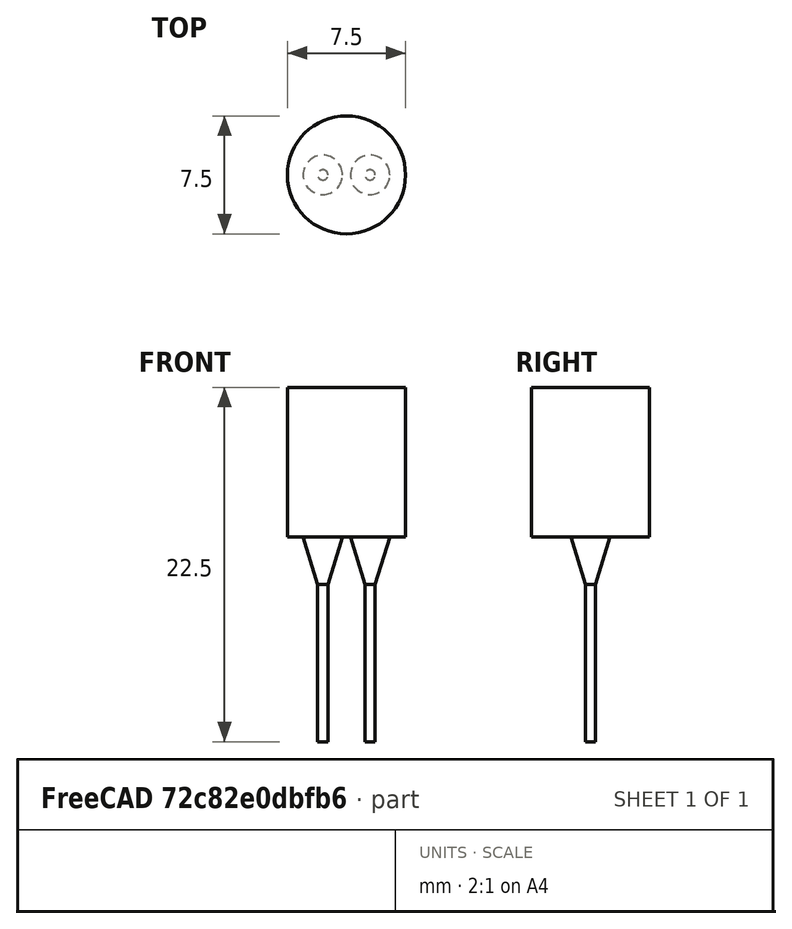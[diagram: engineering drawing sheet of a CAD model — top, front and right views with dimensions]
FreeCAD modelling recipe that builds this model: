
FCSTD DOCUMENT  (FreeCAD 0.19R24366 (Git))
Label:  FERROCORE_COIL0608_inductor_3.0_7.5_9.5
License: All rights reserved
LicenseURL: http://en.wikipedia.org/wiki/All_rights_reserved
objects: Part::Cylinder×3, Part::MultiFuse×3, Part::Cone×2
note: 8 computed .brp shape members not serialized (recipe doc carries the construction recipe); baked Part::Feature solids carry a one-line shape summary decoded from their .brp

FEATURE [Part::Cylinder] Cylinder  label="Henger"
  Angle = 360
  AttacherType = Attacher::AttachEngine3D
  Height = 9.5
  Radius = 3.75
FEATURE [Part::Cone] Cone  label="Kúp"
  Angle = 360
  AttacherType = Attacher::AttachEngine3D
  Height = 3
  Placement = pos=(-9,0,0) rot=(0,0,1;0rad)
  Radius1 = 0.325
  Radius2 = 1.25
FEATURE [Part::Cylinder] Cylinder001  label="Henger001"
  Angle = 360
  AttacherType = Attacher::AttachEngine3D
  Height = 10
  Placement = pos=(-9,0,-10) rot=(0,0,1;0rad)
  Radius = 0.325
FEATURE [Part::MultiFuse] Fusion
  Placement = pos=(10.5,0,-3) rot=(0,0,1;0rad)
  Shapes = -> [Cone,Cylinder001]
FEATURE [Part::Cone] Cone001  label="Kúp001"
  Angle = 360
  AttacherType = Attacher::AttachEngine3D
  Height = 3
  Placement = pos=(-9,0,0) rot=(0,0,1;0rad)
  Radius1 = 0.325
  Radius2 = 1.25
FEATURE [Part::Cylinder] Cylinder002  label="Henger002"
  Angle = 360
  AttacherType = Attacher::AttachEngine3D
  Height = 10
  Placement = pos=(-9,0,-10) rot=(0,0,1;0rad)
  Radius = 0.325
FEATURE [Part::MultiFuse] Fusion001
  Placement = pos=(7.5,0,-3) rot=(0,0,1;0rad)
  Shapes = -> [Cone001,Cylinder002]
FEATURE [Part::MultiFuse] Fusion002
  Shapes = -> [Cylinder,Fusion,Fusion001]
